# Revit family: P1347_2_Hole_Z_Shape_Fitting
name_source: partatom
category: Generic Models
units: mm (PartAtom-declared; Revit-internal decimal feet)

## family parameters
Always vertical = No
Can host rebar = No
Cut with Voids When Loaded = No
OmniClass Number = 23.80.30.17.17
OmniClass Title = Cable Trays and Horizontal Racks
Part Type = Normal
Room Calculation Point = No
Round Connector Dimension = Use Diameter
Shared = No
Work Plane-Based = Yes

## types (5) — shared parameters
Center Distance = 0.813 "
Default Elevation = 48 "
Description = P1347 - 2 Hole Z Shape Fitting
Disclaimer = http://www.unistrut.us
Height = 1.625 "
Hole Diameter = 0.563 "
Length = 3.5 "
Manufacturer = Atkore Unistrut
Model = P1347
Salsify ID1 = US-P1347
Thickness = 0.25 "
Type Comments = 80_77_27_15
URL = https://www.atkore.com
Width = 1.875 "

## per-type parameters (varying)
| type | Material | Power-Strut Part Number | UPC | Weight |
| P1347 EG | Electro Galvanized | PS 647 EG | "78636401994" | 0.55 lbm |
| P1347 HG | Hot Dip Galvanized |  | "786364019963" | 0.58 lbm |
| P1347 GR | Green |  | "786364134703" | 0.55 lbm |
| P1347 SS | Stainless Steel |  | "786364899329" | 0.55 lbm |
| P1347 ST | Stainless Steel |  | "786364055299" | 0.55 lbm |

note: column(s) folded — value = type name in every type: Part Number

## geometry (parser evidence)
native form markers: Sweep x3
no freeform markers — native parametric forms only
